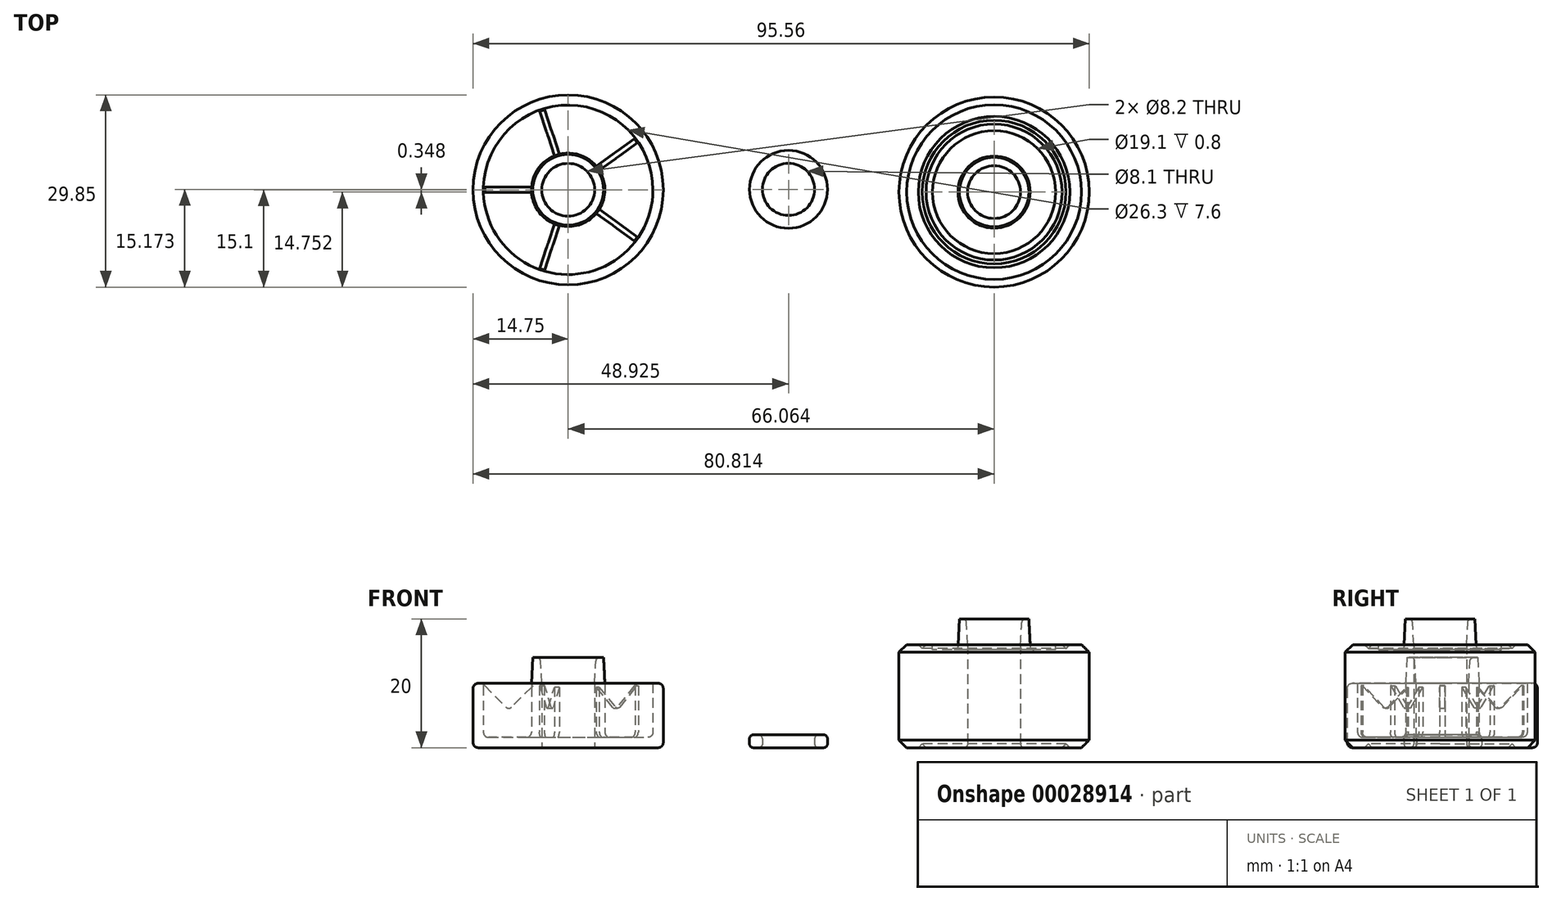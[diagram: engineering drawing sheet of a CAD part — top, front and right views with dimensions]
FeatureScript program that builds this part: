
annotation { "Feature Type Name" : "Feature", "Feature Type Description" : "" }
export const myFeature = defineFeature(function(context is Context, id is Id, definition is map)
    precondition{}
    {
        {
            var Q0;
            Q0=qCreatedBy(makeId("Top.planeOp"),FACE);
            var sketch = newSketch(context, id + "F0", { "sketchPlane" : qUnion([Q0])});
            skCircle(sketch, "E0", {"center": v(0, 0) * mm, "radius": 14.75 * mm});
            skCircle(sketch, "E1", {"center": v(0, 0) * mm, "radius": 4.1 * mm});
            skCircle(sketch, "E2", {"center": v(66.06, -0.35) * mm, "radius": 14.75 * mm});
            skCircle(sketch, "E3", {"center": v(66.06, -0.35) * mm, "radius": 4.1 * mm});
            skCircle(sketch, "E4", {"center": v(34.17, 0.07) * mm, "radius": 4.05 * mm});
            skCircle(sketch, "E5", {"center": v(34.17, 0.07) * mm, "radius": 6.05 * mm});
            skSolve(sketch);
        }
        {
            var Q0;
            Q0=makeQuery(id+"F0.imprint","IMPRINT",FACE,{"disambiguationData":[TD([[makeQuery(id+"F0.imprint","IMPRINT",EDGE,{"derivedFrom":sQuery(id+"F0.wireOp",EDGE,"E0")}),1.0]])]});
            var Q1;
            Q1=makeQuery(id+"F0.imprint","IMPRINT",FACE,{"disambiguationData":[TD([[makeQuery(id+"F0.imprint","IMPRINT",EDGE,{"derivedFrom":sQuery(id+"F0.wireOp",EDGE,"e8e87c0e-89e5-425a-a0b1-75990af84952")}),1.0]])]});
            var Q2;
            Q2=makeQuery(id+"F0.imprint","IMPRINT",FACE,{"disambiguationData":[TD([[makeQuery(id+"F0.imprint","IMPRINT",EDGE,{"derivedFrom":sQuery(id+"F0.wireOp",EDGE,"abde0cf9-1f83-4301-beb9-ac4b5f17cbbd.bottom")}),1.0]])]});
            var Q3;
            Q3=makeQuery(id+"F0.imprint","IMPRINT",FACE,{"disambiguationData":[TD([[makeQuery(id+"F0.imprint","IMPRINT",EDGE,{"derivedFrom":sQuery(id+"F0.wireOp",EDGE,"26bd8618-c4e7-439a-99f6-bb982ce9a2120.MirrorC")}),-1.0]])]});
            var Q4;
            Q4=makeQuery(id+"F0.imprint","IMPRINT",FACE,{"disambiguationData":[TD([[makeQuery(id+"F0.imprint","IMPRINT",EDGE,{"derivedFrom":sQuery(id+"F0.wireOp",EDGE,"45c0c035-0ba1-440d-91dd-f4deb18173680.MirrorC")}),-1.0]])]});
            var Q5;
            Q5=makeQuery(id+"F0.imprint","IMPRINT",FACE,{"disambiguationData":[TD([[makeQuery(id+"F0.imprint","IMPRINT",EDGE,{"derivedFrom":sQuery(id+"F0.wireOp",EDGE,"92f10646-9b55-488a-b265-364474158b900.MirrorCS")}),1.0]])]});
            var Q6;
            {var subQ4=sQuery(id+"F0.wireOp",EDGE,"621f7957-7ed0-4eb6-82c1-ad9769d9a6c72.MirrorCS");Q6=makeQuery(id+"F0.imprint","IMPRINT",FACE,{"disambiguationData":[TD([[makeQuery(id+"F0.imprint","IMPRINT",EDGE,{"derivedFrom":subQ4}),-1.0]])]});}
            var Q7;
            Q7=makeQuery(id+"F0.imprint","IMPRINT",FACE,{"disambiguationData":[TD([[makeQuery(id+"F0.imprint","IMPRINT",EDGE,{"derivedFrom":sQuery(id+"F0.wireOp",EDGE,"621f7957-7ed0-4eb6-82c1-ad9769d9a6c70.MirrorCS")}),-1.0]])]});
            var Q8;
            Q8=makeQuery(id+"F0.imprint","IMPRINT",FACE,{"disambiguationData":[TD([[makeQuery(id+"F0.imprint","IMPRINT",EDGE,{"derivedFrom":sQuery(id+"F0.wireOp",EDGE,"621f7957-7ed0-4eb6-82c1-ad9769d9a6c78.MirrorCS")}),1.0]])]});
            var Q9;
            {var subQ4=sQuery(id+"F0.wireOp",EDGE,"621f7957-7ed0-4eb6-82c1-ad9769d9a6c72.MirrorCS");Q9=makeQuery(id+"F0.imprint","IMPRINT",FACE,{"disambiguationData":[TD([[makeQuery(id+"F0.imprint","IMPRINT",EDGE,{"derivedFrom":subQ4}),1.0]])]});}
            var Q10;
            Q10=makeQuery(id+"F0.imprint","IMPRINT",FACE,{"disambiguationData":[TD([[makeQuery(id+"F0.imprint","IMPRINT",EDGE,{"derivedFrom":sQuery(id+"F0.wireOp",EDGE,"0d3d05c0-9ec0-42d6-8d1c-98659f42b2b8.bottom")}),1.0]])]});
            var Q11;
            Q11=makeQuery(id+"F0.imprint","IMPRINT",FACE,{"disambiguationData":[TD([[makeQuery(id+"F0.imprint","IMPRINT",EDGE,{"derivedFrom":sQuery(id+"F0.wireOp",EDGE,"0d3d05c0-9ec0-42d6-8d1c-98659f42b2b8.bottom")}),1.0]])]});
            extrude(context, id + "F1", {"entities" : qUnion([Q0, Q1, Q2, Q3, Q4, Q5, Q6, Q7, Q8, Q9, Q10, Q11]), "depth" : 10 * mm});
        }
        {
            var Q0;
            Q0=makeQuery(id+"F0.imprint","IMPRINT",FACE,{"disambiguationData":[TD([[makeQuery(id+"F0.imprint","IMPRINT",EDGE,{"derivedFrom":sQuery(id+"F0.wireOp",EDGE,"E2")}),1.0]])]});
            extrude(context, id + "F2", {"entities" : qUnion([Q0]), "depth" : 16 * mm});
        }
        {
            var Q0;
            Q0=makeQuery(id+"F0.imprint","IMPRINT",FACE,{"disambiguationData":[TD([[makeQuery(id+"F0.imprint","IMPRINT",EDGE,{"derivedFrom":sQuery(id+"F0.wireOp",EDGE,"E4")}),-1.0]])]});
            extrude(context, id + "F3", {"entities" : qUnion([Q0]), "depth" : 2 * mm});
        }
        {
            var Q0;
            Q0=makeQuery(id+"F1.opExtrude","CAP_FACE",FACE,{"disambiguationData":[OSD([sQuery(id+"F0.wireOp",EDGE,"E0"),sQuery(id+"F0.wireOp",EDGE,"E1")])],"isStart":false});
            var Q1;
            Q1=makeQuery(id+"F1.opExtrude","CAP_FACE",FACE,{"disambiguationData":[OSD([sQuery(id+"F0.wireOp",EDGE,"b8262d11-0ced-4fc4-a484-381bc9a378e90.MirrorC"),sQuery(id+"F0.wireOp",EDGE,"9f1c5b67-5bd7-481e-852a-bcdd96d4567a0.MirrorC")])],"isStart":false});
            var Q2;
            Q2=makeQuery(id+"F1.opExtrude","CAP_FACE",FACE,{"disambiguationData":[OSD([sQuery(id+"F0.wireOp",EDGE,"e8e87c0e-89e5-425a-a0b1-75990af84952"),sQuery(id+"F0.wireOp",EDGE,"5c285820-c5da-4b27-8afd-64dcaa9398db")])],"isStart":false});
            var Q3;
            Q3=makeQuery(id+"F1.opExtrude","CAP_FACE",FACE,{"disambiguationData":[OSD([sQuery(id+"F0.wireOp",EDGE,"abde0cf9-1f83-4301-beb9-ac4b5f17cbbd.bottom"),sQuery(id+"F0.wireOp",EDGE,"abde0cf9-1f83-4301-beb9-ac4b5f17cbbd.top"),sQuery(id+"F0.wireOp",EDGE,"abde0cf9-1f83-4301-beb9-ac4b5f17cbbd.left"),sQuery(id+"F0.wireOp",EDGE,"abde0cf9-1f83-4301-beb9-ac4b5f17cbbd.right"),sQuery(id+"F0.wireOp",EDGE,"7a9050d6-7617-46cd-b5c2-3b15425381b2"),sQuery(id+"F0.wireOp",EDGE,"b158f154-8a0c-48af-83f9-a2040f8c14ea"),sQuery(id+"F0.wireOp",EDGE,"6b9fe175-4e1e-497c-82d7-d758e1c653ef.filletArc"),sQuery(id+"F0.wireOp",EDGE,"f33478da-a012-4289-b0bd-afe5d81a5774.filletArc"),sQuery(id+"F0.wireOp",EDGE,"24f43b8c-777b-4e50-8554-e1c6360b9280.filletArc"),sQuery(id+"F0.wireOp",EDGE,"1f811094-0bca-45d6-932f-2b620bfc63b1.filletArc")])],"isStart":false});
            var Q4;
            Q4=makeQuery(id+"F1.opExtrude","CAP_FACE",FACE,{"disambiguationData":[OSD([sQuery(id+"F0.wireOp",EDGE,"92f10646-9b55-488a-b265-364474158b900.MirrorCS"),sQuery(id+"F0.wireOp",EDGE,"92f10646-9b55-488a-b265-364474158b901.MirrorCS"),sQuery(id+"F0.wireOp",EDGE,"92f10646-9b55-488a-b265-364474158b902.MirrorCS"),sQuery(id+"F0.wireOp",EDGE,"92f10646-9b55-488a-b265-364474158b903.MirrorCS"),sQuery(id+"F0.wireOp",EDGE,"92f10646-9b55-488a-b265-364474158b904.MirrorC"),sQuery(id+"F0.wireOp",EDGE,"92f10646-9b55-488a-b265-364474158b905.MirrorC"),sQuery(id+"F0.wireOp",EDGE,"92f10646-9b55-488a-b265-364474158b909.MirrorCS"),sQuery(id+"F0.wireOp",EDGE,"92f10646-9b55-488a-b265-364474158b9010.MirrorCS"),sQuery(id+"F0.wireOp",EDGE,"92f10646-9b55-488a-b265-364474158b9011.MirrorCS"),sQuery(id+"F0.wireOp",EDGE,"92f10646-9b55-488a-b265-364474158b9012.MirrorCS")])],"isStart":false});
            var Q5;
            Q5=makeQuery(id+"F1.opExtrude","CAP_FACE",FACE,{"disambiguationData":[OSD([sQuery(id+"F0.wireOp",EDGE,"26bd8618-c4e7-439a-99f6-bb982ce9a2120.MirrorC"),sQuery(id+"F0.wireOp",EDGE,"a178782d-5131-49dc-9e23-0d626eec303c0.MirrorC")])],"isStart":false});
            var Q6;
            Q6=makeQuery(id+"F1.opExtrude","CAP_FACE",FACE,{"disambiguationData":[OSD([sQuery(id+"F0.wireOp",EDGE,"45c0c035-0ba1-440d-91dd-f4deb18173680.MirrorC"),sQuery(id+"F0.wireOp",EDGE,"d4880a5e-9c01-4a5a-914c-df641b7b912d0.MirrorC")])],"isStart":false});
            shell(context, id + "F4", {"entities" : qUnion([Q0, Q1, Q2, Q3, Q4, Q5, Q6]), "thickness" : 1.6 * mm});
        }
        {
            var Q0;
            Q0=makeQuery(id+"F2.opExtrude","CAP_FACE",FACE,{"disambiguationData":[OSD([sQuery(id+"F0.wireOp",EDGE,"E2"),sQuery(id+"F0.wireOp",EDGE,"E3")])],"isStart":false});
            var sketch = newSketch(context, id + "F5", { "sketchPlane" : qUnion([Q0])});
            skCircle(sketch, "E6", {"center": v(66.06, -0.35) * mm, "radius": 5.6 * mm});
            skCircle(sketch, "E7", {"center": v(66.06, -0.35) * mm, "radius": 10.55 * mm});
            skCircle(sketch, "E8", {"center": v(66.06, -0.35) * mm, "radius": 11.75 * mm});
            skCircle(sketch, "E9", {"center": v(66.06, -0.35) * mm, "radius": 9.55 * mm});
            skSolve(sketch);
        }
        {
            var Q0;
            Q0=makeQuery(id+"F0.imprint","IMPRINT",FACE,{"disambiguationData":[TD([[makeQuery(id+"F0.imprint","IMPRINT",EDGE,{"derivedFrom":sQuery(id+"F0.wireOp",EDGE,"E2")}),1.0]])]});
            var sketch = newSketch(context, id + "F6", { "sketchPlane" : qUnion([Q0])});
            skCircle(sketch, "E10", {"center": v(66.06, -0.35) * mm, "radius": 10.55 * mm});
            skCircle(sketch, "E11", {"center": v(66.06, -0.35) * mm, "radius": 11.75 * mm});
            skSolve(sketch);
        }
        {
            var Q0;
            Q0=makeQuery(id+"F5.imprint","IMPRINT",FACE,{"disambiguationData":[TD([[makeQuery(id+"F5.imprint","IMPRINT",EDGE,{"derivedFrom":sQuery(id+"F5.wireOp",EDGE,"E7")}),-1.0]])]});
            extrude(context, id + "F7", {"entities" : qUnion([Q0]), "operationType" : NewBodyOperationType.REMOVE, "oppositeDirection" : true, "depth" : 1.2 * mm, "hasDraft" : true, "draftAngle" : 45 * degree, "draftPullDirection" : true});
        }
        {
            var Q0;
            Q0=makeQuery(id+"F6.imprint","IMPRINT",FACE,{"disambiguationData":[TD([[makeQuery(id+"F6.imprint","IMPRINT",EDGE,{"derivedFrom":sQuery(id+"F6.wireOp",EDGE,"E10")}),-1.0]])]});
            extrude(context, id + "F8", {"entities" : qUnion([Q0]), "operationType" : NewBodyOperationType.REMOVE, "depth" : 1.2 * mm, "hasDraft" : true, "draftAngle" : 45 * degree, "draftPullDirection" : true});
        }
        {
            var Q0;
            Q0=makeQuery(id+"F1.opExtrude","SWEPT_FACE",FACE,{"disambiguationData":[OSD([sQuery(id+"F0.wireOp",EDGE,"26bd8618-c4e7-439a-99f6-bb982ce9a2120.MirrorC")])]});
            var Q1;
            Q1=makeQuery(id+"F1.opExtrude","SWEPT_FACE",FACE,{"disambiguationData":[OSD([sQuery(id+"F0.wireOp",EDGE,"E0")])]});
            var Q2;
            {var subQ0=sQuery(id+"F0.wireOp",EDGE,"E0");var subQ1=sQuery(id+"F0.wireOp",EDGE,"E1");Q2=makeQuery(id+"F4.opShell","OFFSET_FACE",FACE,{"disambiguationData":[OSD([subQ0,subQ1]),TDD([makeQuery(id+"F1.opExtrude","CAP_FACE",FACE,{"disambiguationData":[OSD([subQ0,subQ1])],"isStart":true})])]});}
            var Q3;
            {var subQ0=sQuery(id+"F0.wireOp",EDGE,"26bd8618-c4e7-439a-99f6-bb982ce9a2120.MirrorC");var subQ1=sQuery(id+"F0.wireOp",EDGE,"a178782d-5131-49dc-9e23-0d626eec303c0.MirrorC");Q3=makeQuery(id+"F4.opShell","OFFSET_FACE",FACE,{"disambiguationData":[OSD([subQ0,subQ1]),TDD([makeQuery(id+"F1.opExtrude","CAP_FACE",FACE,{"disambiguationData":[OSD([subQ0,subQ1])],"isStart":true})])]});}
            var Q4;
            {var subQ0=sQuery(id+"F0.wireOp",EDGE,"45c0c035-0ba1-440d-91dd-f4deb18173680.MirrorC");var subQ1=sQuery(id+"F0.wireOp",EDGE,"d4880a5e-9c01-4a5a-914c-df641b7b912d0.MirrorC");Q4=makeQuery(id+"F4.opShell","OFFSET_FACE",FACE,{"disambiguationData":[OSD([subQ0,subQ1]),TDD([makeQuery(id+"F1.opExtrude","CAP_FACE",FACE,{"disambiguationData":[OSD([subQ0,subQ1])],"isStart":true})])]});}
            var Q5;
            {var subQ0=sQuery(id+"F0.wireOp",EDGE,"e8e87c0e-89e5-425a-a0b1-75990af84952");var subQ1=sQuery(id+"F0.wireOp",EDGE,"5c285820-c5da-4b27-8afd-64dcaa9398db");Q5=makeQuery(id+"F4.opShell","OFFSET_FACE",FACE,{"disambiguationData":[OSD([subQ0,subQ1]),TDD([makeQuery(id+"F1.opExtrude","CAP_FACE",FACE,{"disambiguationData":[OSD([subQ0,subQ1])],"isStart":true})])]});}
            var Q6;
            Q6=makeQuery(id+"F1.opExtrude","SWEPT_FACE",FACE,{"disambiguationData":[OSD([sQuery(id+"F0.wireOp",EDGE,"92f10646-9b55-488a-b265-364474158b909.MirrorCS")])]});
            var Q7;
            Q7=makeQuery(id+"F1.opExtrude","CAP_EDGE",EDGE,{"disambiguationData":[OSD([sQuery(id+"F0.wireOp",EDGE,"5c285820-c5da-4b27-8afd-64dcaa9398db")])],"isStart":false});
            var Q8;
            Q8=makeQuery(id+"F1.opExtrude","CAP_EDGE",EDGE,{"disambiguationData":[OSD([sQuery(id+"F0.wireOp",EDGE,"d4880a5e-9c01-4a5a-914c-df641b7b912d0.MirrorC")])],"isStart":false});
            var Q9;
            Q9=makeQuery(id+"F1.opExtrude","SWEPT_FACE",FACE,{"disambiguationData":[OSD([sQuery(id+"F0.wireOp",EDGE,"abde0cf9-1f83-4301-beb9-ac4b5f17cbbd.right")])]});
            var Q10;
            Q10=makeQuery(id+"F1.opExtrude","CAP_EDGE",EDGE,{"disambiguationData":[OSD([sQuery(id+"F0.wireOp",EDGE,"45c0c035-0ba1-440d-91dd-f4deb18173680.MirrorC")])],"isStart":false});
            var Q11;
            Q11=makeQuery(id+"F1.opExtrude","CAP_EDGE",EDGE,{"disambiguationData":[OSD([sQuery(id+"F0.wireOp",EDGE,"e8e87c0e-89e5-425a-a0b1-75990af84952")])],"isStart":false});
            var Q12;
            {var subQ0=sQuery(id+"F0.wireOp",EDGE,"92f10646-9b55-488a-b265-364474158b900.MirrorCS");var subQ1=sQuery(id+"F0.wireOp",EDGE,"92f10646-9b55-488a-b265-364474158b901.MirrorCS");var subQ2=sQuery(id+"F0.wireOp",EDGE,"92f10646-9b55-488a-b265-364474158b902.MirrorCS");var subQ3=sQuery(id+"F0.wireOp",EDGE,"92f10646-9b55-488a-b265-364474158b903.MirrorCS");var subQ4=sQuery(id+"F0.wireOp",EDGE,"92f10646-9b55-488a-b265-364474158b904.MirrorC");var subQ5=sQuery(id+"F0.wireOp",EDGE,"92f10646-9b55-488a-b265-364474158b905.MirrorC");var subQ6=sQuery(id+"F0.wireOp",EDGE,"92f10646-9b55-488a-b265-364474158b909.MirrorCS");var subQ7=sQuery(id+"F0.wireOp",EDGE,"92f10646-9b55-488a-b265-364474158b9010.MirrorCS");var subQ8=sQuery(id+"F0.wireOp",EDGE,"92f10646-9b55-488a-b265-364474158b9011.MirrorCS");var subQ9=sQuery(id+"F0.wireOp",EDGE,"92f10646-9b55-488a-b265-364474158b9012.MirrorCS");Q12=makeQuery(id+"F4.opShell","OFFSET_FACE",FACE,{"disambiguationData":[OSD([subQ0,subQ1,subQ2,subQ3,subQ4,subQ5,subQ6,subQ7,subQ8,subQ9]),TDD([makeQuery(id+"F1.opExtrude","CAP_FACE",FACE,{"disambiguationData":[OSD([subQ0,subQ1,subQ2,subQ3,subQ4,subQ5,subQ6,subQ7,subQ8,subQ9])],"isStart":true})])]});}
            var Q13;
            {var subQ0=sQuery(id+"F0.wireOp",EDGE,"abde0cf9-1f83-4301-beb9-ac4b5f17cbbd.bottom");var subQ1=sQuery(id+"F0.wireOp",EDGE,"abde0cf9-1f83-4301-beb9-ac4b5f17cbbd.top");var subQ2=sQuery(id+"F0.wireOp",EDGE,"abde0cf9-1f83-4301-beb9-ac4b5f17cbbd.left");var subQ3=sQuery(id+"F0.wireOp",EDGE,"abde0cf9-1f83-4301-beb9-ac4b5f17cbbd.right");var subQ4=sQuery(id+"F0.wireOp",EDGE,"7a9050d6-7617-46cd-b5c2-3b15425381b2");var subQ5=sQuery(id+"F0.wireOp",EDGE,"b158f154-8a0c-48af-83f9-a2040f8c14ea");var subQ6=sQuery(id+"F0.wireOp",EDGE,"6b9fe175-4e1e-497c-82d7-d758e1c653ef.filletArc");var subQ7=sQuery(id+"F0.wireOp",EDGE,"f33478da-a012-4289-b0bd-afe5d81a5774.filletArc");var subQ8=sQuery(id+"F0.wireOp",EDGE,"24f43b8c-777b-4e50-8554-e1c6360b9280.filletArc");var subQ9=sQuery(id+"F0.wireOp",EDGE,"1f811094-0bca-45d6-932f-2b620bfc63b1.filletArc");Q13=makeQuery(id+"F4.opShell","OFFSET_FACE",FACE,{"disambiguationData":[OSD([subQ0,subQ1,subQ2,subQ3,subQ4,subQ5,subQ6,subQ7,subQ8,subQ9]),TDD([makeQuery(id+"F1.opExtrude","CAP_FACE",FACE,{"disambiguationData":[OSD([subQ0,subQ1,subQ2,subQ3,subQ4,subQ5,subQ6,subQ7,subQ8,subQ9])],"isStart":true})])]});}
            fillet(context, id + "F9", {"entities" : qUnion([Q0, Q1, Q2, Q3, Q4, Q5, Q6, Q7, Q8, Q9, Q10, Q11, Q12, Q13]), "radius" : 0.8 * mm, "tangentPropagation" : true, "allowEdgeOverflow" : false});
        }
        {
            var Q0;
            Q0=makeQuery(id+"F2.opExtrude","CAP_EDGE",EDGE,{"disambiguationData":[OSD([sQuery(id+"F0.wireOp",EDGE,"E2")])],"isStart":true});
            var Q1;
            Q1=makeQuery(id+"F2.opExtrude","CAP_EDGE",EDGE,{"disambiguationData":[OSD([sQuery(id+"F0.wireOp",EDGE,"E2")])],"isStart":false});
            chamfer(context, id + "F10", {"entities" : qUnion([Q0, Q1]), "width" : 1.2 * mm, "tangentPropagation" : true});
        }
        {
            var Q0;
            {var subQ0=sQuery(id+"F0.wireOp",EDGE,"26bd8618-c4e7-439a-99f6-bb982ce9a2120.MirrorC");var subQ1=sQuery(id+"F0.wireOp",EDGE,"a178782d-5131-49dc-9e23-0d626eec303c0.MirrorC");Q0=makeQuery(id+"F4.opShell","OFFSET_FACE",FACE,{"disambiguationData":[OSD([subQ0,subQ1]),TDD([makeQuery(id+"F1.opExtrude","CAP_FACE",FACE,{"disambiguationData":[OSD([subQ0,subQ1])],"isStart":false})])]});}
            var Q1;
            {var subQ0=sQuery(id+"F0.wireOp",EDGE,"E0");var subQ1=sQuery(id+"F0.wireOp",EDGE,"E1");Q1=makeQuery(id+"F4.opShell","OFFSET_FACE",FACE,{"disambiguationData":[OSD([subQ0,subQ1]),TDD([makeQuery(id+"F1.opExtrude","CAP_FACE",FACE,{"disambiguationData":[OSD([subQ0,subQ1])],"isStart":false})])]});}
            var Q2;
            Q2=makeQuery(id+"F1.opExtrude","CAP_FACE",FACE,{"disambiguationData":[OSD([sQuery(id+"F0.wireOp",EDGE,"0d3d05c0-9ec0-42d6-8d1c-98659f42b2b8.bottom"),sQuery(id+"F0.wireOp",EDGE,"0d3d05c0-9ec0-42d6-8d1c-98659f42b2b8.top"),sQuery(id+"F0.wireOp",EDGE,"0d3d05c0-9ec0-42d6-8d1c-98659f42b2b8.left"),sQuery(id+"F0.wireOp",EDGE,"0d3d05c0-9ec0-42d6-8d1c-98659f42b2b8.right"),sQuery(id+"F0.wireOp",EDGE,"b5ff977a-650c-4230-9985-ae6901ddbf3c.bottom"),sQuery(id+"F0.wireOp",EDGE,"b5ff977a-650c-4230-9985-ae6901ddbf3c.top"),sQuery(id+"F0.wireOp",EDGE,"b5ff977a-650c-4230-9985-ae6901ddbf3c.left"),sQuery(id+"F0.wireOp",EDGE,"b5ff977a-650c-4230-9985-ae6901ddbf3c.right")])],"isStart":false});
            var Q3;
            Q3=makeQuery(id+"F5.imprint","IMPRINT",FACE,{"disambiguationData":[TD([[makeQuery(id+"F5.imprint","IMPRINT",EDGE,{"derivedFrom":sQuery(id+"F5.wireOp",EDGE,"E6")}),1.0]])]});
            extrude(context, id + "F11", {"entities" : qUnion([Q0, Q1, Q2, Q3]), "operationType" : NewBodyOperationType.ADD, "depth" : 4 * mm, "hasDraft" : true, "draftAngle" : 3 * degree, "draftPullDirection" : true});
        }
        {
            var Q0;
            Q0=makeQuery(id+"F5.imprint","IMPRINT",FACE,{"disambiguationData":[TD([[makeQuery(id+"F5.imprint","IMPRINT",EDGE,{"derivedFrom":sQuery(id+"F5.wireOp",EDGE,"E6")}),-1.0]])]});
            extrude(context, id + "F12", {"entities" : qUnion([Q0]), "operationType" : NewBodyOperationType.REMOVE, "oppositeDirection" : true, "depth" : 0.8 * mm});
        }
        {
            var Q0;
            {var subQ0=sQuery(id+"F0.wireOp",EDGE,"E0");var subQ1=sQuery(id+"F0.wireOp",EDGE,"E1");Q0=makeQuery(id+"F4.opShell","OFFSET_FACE",FACE,{"disambiguationData":[OSD([subQ0,subQ1]),TDD([makeQuery(id+"F1.opExtrude","CAP_FACE",FACE,{"disambiguationData":[OSD([subQ0,subQ1])],"isStart":true})])]});}
            var sketch = newSketch(context, id + "F13", { "sketchPlane" : qUnion([Q0])});
            skLineSegment(sketch, "E12", {"start": v(-5.48, 0.4) * mm, "end": v(-13.94, 0.4) * mm});
            skLineSegment(sketch, "E13", {"start": v(-13.94, 0.4) * mm, "end": v(-13.94, -0.4) * mm});
            skLineSegment(sketch, "E14", {"start": v(-13.94, -0.4) * mm, "end": v(-5.48, -0.4) * mm});
            skLineSegment(sketch, "E15", {"start": v(-5.48, 0.4) * mm, "end": v(-5.48, -0.4) * mm});
            skSolve(sketch);
        }
        {
            var Q0;
            {var subQ0=sQuery(id+"F0.wireOp",EDGE,"E1");var subQ1=sQuery(id+"F0.wireOp",EDGE,"E0");var subQ2=makeQuery(id+"F4.opShell","OFFSET_FACE",FACE,{"disambiguationData":[OSD([subQ1,subQ0]),TDD([makeQuery(id+"F1.opExtrude","CAP_FACE",FACE,{"disambiguationData":[OSD([subQ1,subQ0])],"isStart":true})])]});var subQ3=makeQuery(id+"F9.opFillet","BLEND_EDGE",EDGE,{"blendedFrom":[makeQuery(id+"F4.opShell","OFFSET_EDGE",EDGE,{"disambiguationData":[OSD([subQ0]),TDD([makeQuery(id+"F1.opExtrude","CAP_EDGE",EDGE,{"disambiguationData":[OSD([subQ0])],"isStart":true})])]}),subQ2],"blendedInto":[subQ2]});var subQ6=sQuery(id+"F13.wireOp",EDGE,"E12");var subQ7=makeQuery(id+"F13.imprint","INTERSECT",VERTEX,{"derivedFrom":[subQ3,subQ6]});Q0=makeQuery(id+"F13.imprint","IMPRINT",FACE,{"disambiguationData":[TD([[makeQuery(id+"F13.imprint","IMPRINT",EDGE,{"disambiguationData":[TD([[subQ7,-1.0]])],"derivedFrom":subQ6}),1.0]])]});}
            var Q1;
            {var subQ7=sQuery(id+"F13.wireOp",EDGE,"E13");Q1=makeQuery(id+"F13.imprint","IMPRINT",FACE,{"disambiguationData":[TD([[makeQuery(id+"F13.imprint","IMPRINT",EDGE,{"derivedFrom":subQ7}),1.0]])]});}
            var Q2;
            {var subQ7=sQuery(id+"F13.wireOp",EDGE,"E15");Q2=makeQuery(id+"F13.imprint","IMPRINT",FACE,{"disambiguationData":[TD([[makeQuery(id+"F13.imprint","IMPRINT",EDGE,{"derivedFrom":subQ7}),-1.0]])]});}
            extrude(context, id + "F14", {"entities" : qUnion([Q0, Q1, Q2]), "depth" : 8 * mm});
        }
        {
            var Q0;
            Q0=makeQuery(id+"F14.opExtrude","SWEPT_FACE",FACE,{"disambiguationData":[OSD([sQuery(id+"F13.wireOp",EDGE,"E14")])]});
            var sketch = newSketch(context, id + "F15", { "sketchPlane" : qUnion([Q0])});
            skLineSegment(sketch, "E16", {"start": v(-9.21, 5.87) * mm, "end": v(-5.48, 9.6) * mm});
            skLineSegment(sketch, "E17", {"start": v(-12.94, 9.6) * mm, "end": v(-9.21, 5.87) * mm});
            skLineSegment(sketch, "E18", {"start": v(-13.94, 9.6) * mm, "end": v(-12.94, 9.6) * mm});
            skSolve(sketch);
        }
        {
            var Q0;
            {var subQ3=sQuery(id+"F15.wireOp",EDGE,"E16");Q0=makeQuery(id+"F15.imprint","IMPRINT",FACE,{"disambiguationData":[TD([[makeQuery(id+"F15.imprint","IMPRINT",EDGE,{"derivedFrom":subQ3}),1.0]])]});}
            extrude(context, id + "F16", {"entities" : qUnion([Q0]), "operationType" : NewBodyOperationType.REMOVE, "endBound" : BoundingType.UP_TO_NEXT, "oppositeDirection" : true, "depth" : 2 * mm});
        }
        {
            var Q0;
            Q0=makeQuery(id+"F16.boolean.opBoolean","COPY",EDGE,{"derivedFrom":makeQuery(id+"F16.opExtrude","SWEPT_EDGE",EDGE,{"disambiguationData":[OSD([sQuery(id+"F15.wireOp",EDGE,"E16"),sQuery(id+"F15.wireOp",EDGE,"E17")])]})});
            var Q1;
            {var subQ0=sQuery(id+"F0.wireOp",EDGE,"E1");Q1=makeQuery(id+"F11.opExtrude","CAP_EDGE",EDGE,{"disambiguationData":[OSD([subQ0]),TDD([makeQuery(id+"F1.opExtrude","CAP_EDGE",EDGE,{"disambiguationData":[OSD([subQ0])],"isStart":false})])],"isStart":false});}
            var Q2;
            Q2=makeQuery(id+"F11.opExtrude","CAP_EDGE",EDGE,{"disambiguationData":[OSD([sQuery(id+"F0.wireOp",EDGE,"E3")])],"isStart":false});
            var Q3;
            Q3=makeQuery(id+"F2.opExtrude","CAP_EDGE",EDGE,{"disambiguationData":[OSD([sQuery(id+"F0.wireOp",EDGE,"E3")])],"isStart":true});
            var Q4;
            Q4=makeQuery(id+"F12.boolean.opBoolean","COPY",EDGE,{"derivedFrom":makeQuery(id+"F12.opExtrude","CAP_EDGE",EDGE,{"disambiguationData":[OSD([sQuery(id+"F5.wireOp",EDGE,"E9")])],"isStart":true})});
            var Q5;
            Q5=makeQuery(id+"F12.boolean.opBoolean","COPY",EDGE,{"derivedFrom":makeQuery(id+"F12.opExtrude","CAP_EDGE",EDGE,{"disambiguationData":[OSD([sQuery(id+"F5.wireOp",EDGE,"E6")])],"isStart":false})});
            var Q6;
            Q6=makeQuery(id+"F3.opExtrude","CAP_EDGE",EDGE,{"disambiguationData":[OSD([sQuery(id+"F0.wireOp",EDGE,"E4")])],"isStart":false});
            var Q7;
            Q7=makeQuery(id+"F3.opExtrude","CAP_EDGE",EDGE,{"disambiguationData":[OSD([sQuery(id+"F0.wireOp",EDGE,"E5")])],"isStart":true});
            var Q8;
            Q8=makeQuery(id+"F3.opExtrude","CAP_EDGE",EDGE,{"disambiguationData":[OSD([sQuery(id+"F0.wireOp",EDGE,"E4")])],"isStart":true});
            var Q9;
            Q9=makeQuery(id+"F3.opExtrude","CAP_EDGE",EDGE,{"disambiguationData":[OSD([sQuery(id+"F0.wireOp",EDGE,"E5")])],"isStart":false});
            fillet(context, id + "F17", {"entities" : qUnion([Q0, Q1, Q2, Q3, Q4, Q5, Q6, Q7, Q8, Q9]), "radius" : 0.6 * mm, "tangentPropagation" : true, "allowEdgeOverflow" : false});
        }
        {
            var Q0;
            Q0=qCreatedBy(makeId("Front.planeOp"),FACE);
            var sketch = newSketch(context, id + "F18", { "sketchPlane" : qUnion([Q0])});
            skLineSegment(sketch, "E19", {"start": v(0, 28.76) * mm, "end": v(0, -19.5) * mm, "construction": true});
            skSolve(sketch);
        }
        {
            var Q0;
            Q0=makeQuery(id+"F14.opExtrude","SWEPT_BODY",BODY,{"disambiguationData":[OSD([sQuery(id+"F13.wireOp",EDGE,"E12"),sQuery(id+"F13.wireOp",EDGE,"E13"),sQuery(id+"F13.wireOp",EDGE,"E14"),sQuery(id+"F13.wireOp",EDGE,"E15")])]});
            var Q1;
            Q1=sQuery(id+"F18.wireOp",EDGE,"E19");
            var Q2;
            Q2=makeQuery(id+"F1.opExtrude","SWEPT_BODY",BODY,{"disambiguationData":[OSD([sQuery(id+"F0.wireOp",EDGE,"E0"),sQuery(id+"F0.wireOp",EDGE,"E1")])]});
            circularPattern(context, id + "F19", {"operationType" : NewBodyOperationType.ADD, "entities" : qUnion([Q0]), "axis" : qUnion([Q1]), "angle" : 72 * degree, "instanceCount" : 5});
        }
    });
